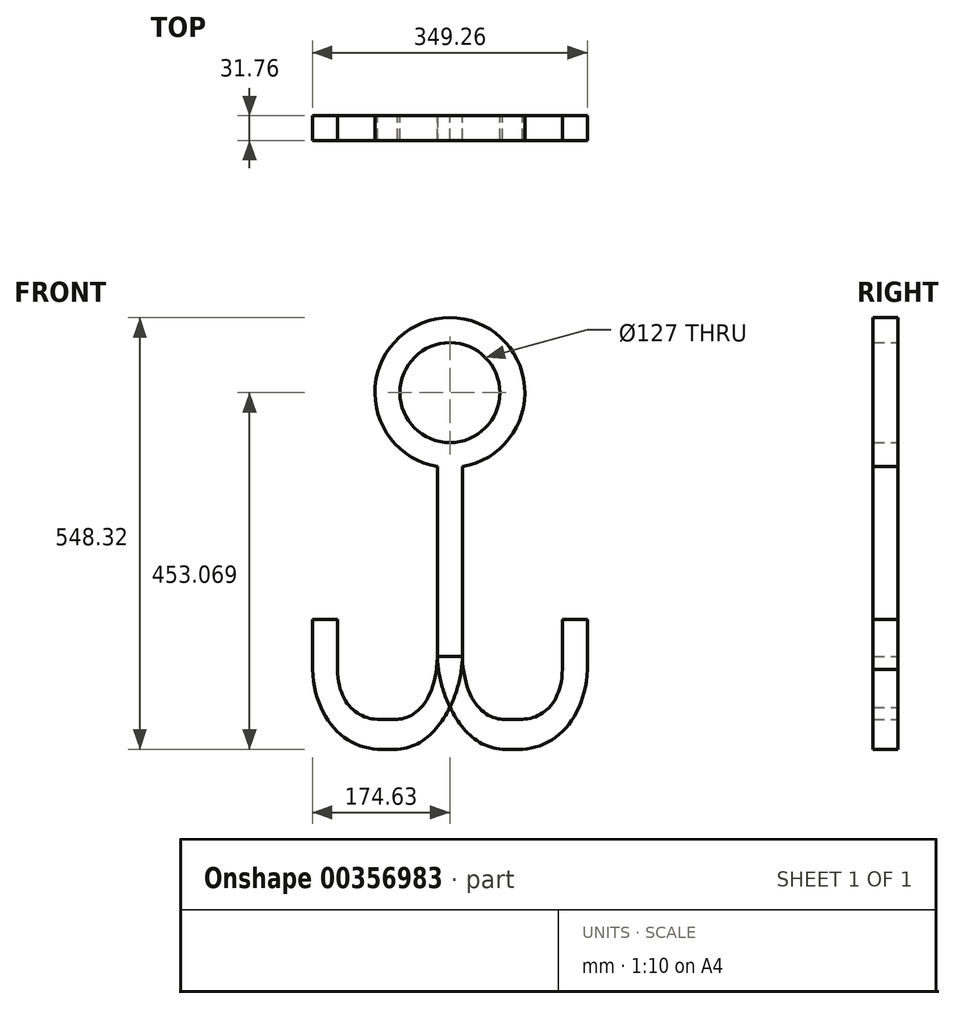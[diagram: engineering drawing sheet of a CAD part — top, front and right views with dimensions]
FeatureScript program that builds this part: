
annotation { "Feature Type Name" : "Feature", "Feature Type Description" : "" }
export const myFeature = defineFeature(function(context is Context, id is Id, definition is map)
    precondition{}
    {
        {
            var Q0;
            Q0=qCreatedBy(makeId("Front.planeOp"),FACE);
            var sketch = newSketch(context, id + "F0", { "sketchPlane" : qUnion([Q0])});
            skLineSegment(sketch, "E0.bottom", {"start": v(-15.88, -345.2) * mm, "end": v(15.88, -345.2) * mm});
            skLineSegment(sketch, "E0.top", {"start": v(-15.87, -91.2) * mm, "end": v(15.87, -91.2) * mm});
            skLineSegment(sketch, "E0.left", {"start": v(-15.88, -345.2) * mm, "end": v(-15.87, -91.2) * mm});
            skLineSegment(sketch, "E0.right", {"start": v(15.87, -345.2) * mm, "end": v(15.88, -91.2) * mm});
            skPoint(sketch, "E0.middle", {"position": v(0, -218.2) * mm});
            skLineSegment(sketch, "E1.bottom", {"start": v(66.68, -424.89) * mm, "end": v(92.08, -424.89) * mm});
            skLineSegment(sketch, "E1.top", {"start": v(66.68, -462.99) * mm, "end": v(92.08, -462.99) * mm});
            skLineSegment(sketch, "E1.left", {"start": v(66.68, -424.89) * mm, "end": v(66.68, -462.99) * mm});
            skLineSegment(sketch, "E1.right", {"start": v(92.08, -424.89) * mm, "end": v(92.08, -462.99) * mm});
            skPoint(sketch, "E1.middle", {"position": v(79.38, -443.94) * mm});
            skLineSegment(sketch, "E2.bottom", {"start": v(174.62, -361.39) * mm, "end": v(142.88, -361.39) * mm});
            skLineSegment(sketch, "E2.top", {"start": v(174.62, -297.89) * mm, "end": v(142.88, -297.89) * mm});
            skLineSegment(sketch, "E2.left", {"start": v(174.63, -361.39) * mm, "end": v(174.63, -297.89) * mm});
            skLineSegment(sketch, "E2.right", {"start": v(142.88, -361.39) * mm, "end": v(142.88, -297.89) * mm});
            skPoint(sketch, "E2.middle", {"position": v(158.75, -329.64) * mm});
            skCircle(sketch, "E3", {"center": v(0, -9.92) * mm, "radius": 95.25 * mm});
            skCircle(sketch, "E4", {"center": v(0, -9.92) * mm, "radius": 63.5 * mm});
            skLineSegment(sketch, "E5", {"start": v(0, 0) * mm, "end": v(0, -345.2) * mm});
            skLineSegment(sketch, "E6.MirrorCS", {"start": v(15.88, -345.2) * mm, "end": v(-15.88, -345.2) * mm});
            skLineSegment(sketch, "E7.MirrorCS", {"start": v(-66.68, -424.89) * mm, "end": v(-66.68, -462.99) * mm});
            skLineSegment(sketch, "E8.MirrorCS", {"start": v(-66.68, -462.99) * mm, "end": v(-92.08, -462.99) * mm});
            skLineSegment(sketch, "E9.MirrorCS", {"start": v(-66.68, -424.89) * mm, "end": v(-92.08, -424.89) * mm});
            skLineSegment(sketch, "E10.MirrorCS", {"start": v(-92.08, -424.89) * mm, "end": v(-92.08, -462.99) * mm});
            skLineSegment(sketch, "E11.MirrorCS", {"start": v(-174.62, -361.39) * mm, "end": v(-142.88, -361.39) * mm});
            skLineSegment(sketch, "E12.MirrorCS", {"start": v(-174.62, -297.89) * mm, "end": v(-142.88, -297.89) * mm});
            skLineSegment(sketch, "E13.MirrorCS", {"start": v(-142.88, -361.39) * mm, "end": v(-142.88, -297.89) * mm});
            skLineSegment(sketch, "E14.MirrorCS", {"start": v(-174.62, -361.39) * mm, "end": v(-174.62, -297.89) * mm});
            skPoint(sketch, "E15.MirrorP", {"position": v(-158.75, -329.64) * mm});
            skPoint(sketch, "E16.MirrorP", {"position": v(-79.38, -443.94) * mm});
            skFitSpline(sketch, "E17", {"points": [v(-66.67, -462.99) * mm, v(15.88, -345.2) * mm], "startDerivative": vector(162.73, 9.04) * mm, "endDerivative": vector(1.02, 130.09) * mm});
            skFitSpline(sketch, "E18", {"points": [v(-66.67, -424.89) * mm, v(-15.88, -345.2) * mm], "startDerivative": vector(65.94, 3.15) * mm, "endDerivative": vector(5.15, 171.39) * mm});
            skFitSpline(sketch, "E19", {"points": [v(-174.62, -361.39) * mm, v(-92.07, -462.99) * mm], "startDerivative": vector(7.09, -178.32) * mm, "endDerivative": vector(133.44, -7.74) * mm});
            skFitSpline(sketch, "E20", {"points": [v(-142.87, -361.39) * mm, v(-92.07, -424.89) * mm], "startDerivative": vector(2.18, -127.98) * mm, "endDerivative": vector(77.94, -3.15) * mm});
            skFitSpline(sketch, "E21.MirrorCS", {"points": [v(66.67, -462.99) * mm, v(-15.88, -345.2) * mm], "startDerivative": vector(-162.73, 9.04) * mm, "endDerivative": vector(-1.02, 130.09) * mm});
            skFitSpline(sketch, "E22.MirrorCS", {"points": [v(66.67, -424.89) * mm, v(15.88, -345.2) * mm], "startDerivative": vector(-65.94, 3.15) * mm, "endDerivative": vector(-5.15, 171.39) * mm});
            skFitSpline(sketch, "E23.MirrorCS", {"points": [v(142.88, -361.39) * mm, v(92.07, -424.89) * mm], "startDerivative": vector(-2.18, -127.98) * mm, "endDerivative": vector(-77.94, -3.15) * mm});
            skFitSpline(sketch, "E24.MirrorCS", {"points": [v(174.63, -361.39) * mm, v(92.07, -462.99) * mm], "startDerivative": vector(-7.09, -178.32) * mm, "endDerivative": vector(-133.44, -7.74) * mm});
            skSolve(sketch);
        }
        {
            var Q0;
            {var subQ0=sQuery(id+"F0.wireOp",EDGE,"E0.left");var subQ1=sQuery(id+"F0.wireOp",EDGE,"E0.top");var subQ2=makeQuery(id+"F0.imprint","INTERSECT",VERTEX,{"derivedFrom":[subQ1,subQ0]});Q0=makeQuery(id+"F0.imprint","IMPRINT",FACE,{"disambiguationData":[TD([[makeQuery(id+"F0.imprint","IMPRINT",EDGE,{"disambiguationData":[TD([[subQ2,-1.0]])],"derivedFrom":subQ1}),1.0]])]});}
            var Q1;
            {var subQ1=sQuery(id+"F0.wireOp",EDGE,"E0.right");var subQ3=sQuery(id+"F0.wireOp",EDGE,"E3");var subQ4=makeQuery(id+"F0.imprint","INTERSECT",VERTEX,{"derivedFrom":[subQ1,subQ3]});Q1=makeQuery(id+"F0.imprint","IMPRINT",FACE,{"disambiguationData":[TD([[makeQuery(id+"F0.imprint","IMPRINT",EDGE,{"disambiguationData":[TD([[subQ4,1.0]])],"derivedFrom":subQ3}),-1.0]])]});}
            var Q2;
            {var subQ0=sQuery(id+"F0.wireOp",EDGE,"E0.left");var subQ1=sQuery(id+"F0.wireOp",EDGE,"E0.top");var subQ2=makeQuery(id+"F0.imprint","INTERSECT",VERTEX,{"derivedFrom":[subQ1,subQ0]});Q2=makeQuery(id+"F0.imprint","IMPRINT",FACE,{"disambiguationData":[TD([[makeQuery(id+"F0.imprint","IMPRINT",EDGE,{"disambiguationData":[TD([[subQ2,-1.0]])],"derivedFrom":subQ1}),-1.0]])]});}
            var Q3;
            {var subQ0=sQuery(id+"F0.wireOp",EDGE,"E0.right");var subQ1=sQuery(id+"F0.wireOp",EDGE,"E0.top");var subQ2=makeQuery(id+"F0.imprint","INTERSECT",VERTEX,{"derivedFrom":[subQ1,subQ0]});Q3=makeQuery(id+"F0.imprint","IMPRINT",FACE,{"disambiguationData":[TD([[makeQuery(id+"F0.imprint","IMPRINT",EDGE,{"disambiguationData":[TD([[subQ2,1.0]])],"derivedFrom":subQ1}),-1.0]])]});}
            var Q4;
            {var subQ1=sQuery(id+"F0.wireOp",EDGE,"E0.left");var subQ3=sQuery(id+"F0.wireOp",EDGE,"E3");var subQ4=makeQuery(id+"F0.imprint","INTERSECT",VERTEX,{"derivedFrom":[subQ1,subQ3]});Q4=makeQuery(id+"F0.imprint","IMPRINT",FACE,{"disambiguationData":[TD([[makeQuery(id+"F0.imprint","IMPRINT",EDGE,{"disambiguationData":[TD([[subQ4,-1.0]])],"derivedFrom":subQ3}),-1.0]])]});}
            var Q5;
            {var subQ1=sQuery(id+"F0.wireOp",EDGE,"E6.MirrorCS");var subQ3=makeQuery(id+"F0.imprint","INTERSECT",VERTEX,{"derivedFrom":[sQuery(id+"F0.wireOp",EDGE,"E5"),subQ1]});Q5=makeQuery(id+"F0.imprint","IMPRINT",FACE,{"disambiguationData":[TD([[makeQuery(id+"F0.imprint","IMPRINT",EDGE,{"disambiguationData":[TD([[subQ3,1.0]])],"derivedFrom":subQ1}),1.0]])]});}
            var Q6;
            {var subQ0=sQuery(id+"F0.wireOp",EDGE,"E7.MirrorCS");Q6=makeQuery(id+"F0.imprint","IMPRINT",FACE,{"disambiguationData":[TD([[makeQuery(id+"F0.imprint","IMPRINT",EDGE,{"derivedFrom":subQ0}),1.0]])]});}
            var Q7;
            Q7=makeQuery(id+"F0.imprint","IMPRINT",FACE,{"disambiguationData":[TD([[makeQuery(id+"F0.imprint","IMPRINT",EDGE,{"derivedFrom":sQuery(id+"F0.wireOp",EDGE,"E7.MirrorCS")}),-1.0]])]});
            var Q8;
            Q8=makeQuery(id+"F0.imprint","IMPRINT",FACE,{"disambiguationData":[TD([[makeQuery(id+"F0.imprint","IMPRINT",EDGE,{"derivedFrom":sQuery(id+"F0.wireOp",EDGE,"E10.MirrorCS")}),-1.0]])]});
            var Q9;
            Q9=makeQuery(id+"F0.imprint","IMPRINT",FACE,{"disambiguationData":[TD([[makeQuery(id+"F0.imprint","IMPRINT",EDGE,{"derivedFrom":sQuery(id+"F0.wireOp",EDGE,"E11.MirrorCS")}),1.0]])]});
            var Q10;
            {var subQ0=sQuery(id+"F0.wireOp",EDGE,"E1.left");Q10=makeQuery(id+"F0.imprint","IMPRINT",FACE,{"disambiguationData":[TD([[makeQuery(id+"F0.imprint","IMPRINT",EDGE,{"derivedFrom":subQ0}),-1.0]])]});}
            var Q11;
            Q11=makeQuery(id+"F0.imprint","IMPRINT",FACE,{"disambiguationData":[TD([[makeQuery(id+"F0.imprint","IMPRINT",EDGE,{"derivedFrom":sQuery(id+"F0.wireOp",EDGE,"E1.bottom")}),-1.0]])]});
            var Q12;
            Q12=makeQuery(id+"F0.imprint","IMPRINT",FACE,{"disambiguationData":[TD([[makeQuery(id+"F0.imprint","IMPRINT",EDGE,{"derivedFrom":sQuery(id+"F0.wireOp",EDGE,"E1.right")}),1.0]])]});
            var Q13;
            Q13=makeQuery(id+"F0.imprint","IMPRINT",FACE,{"disambiguationData":[TD([[makeQuery(id+"F0.imprint","IMPRINT",EDGE,{"derivedFrom":sQuery(id+"F0.wireOp",EDGE,"E2.bottom")}),-1.0]])]});
            extrude(context, id + "F1", {"entities" : qUnion([Q0, Q1, Q2, Q3, Q4, Q5, Q6, Q7, Q8, Q9, Q10, Q11, Q12, Q13]), "endBound" : BoundingType.SYMMETRIC, "depth" : 31.75 * mm});
        }
    });
